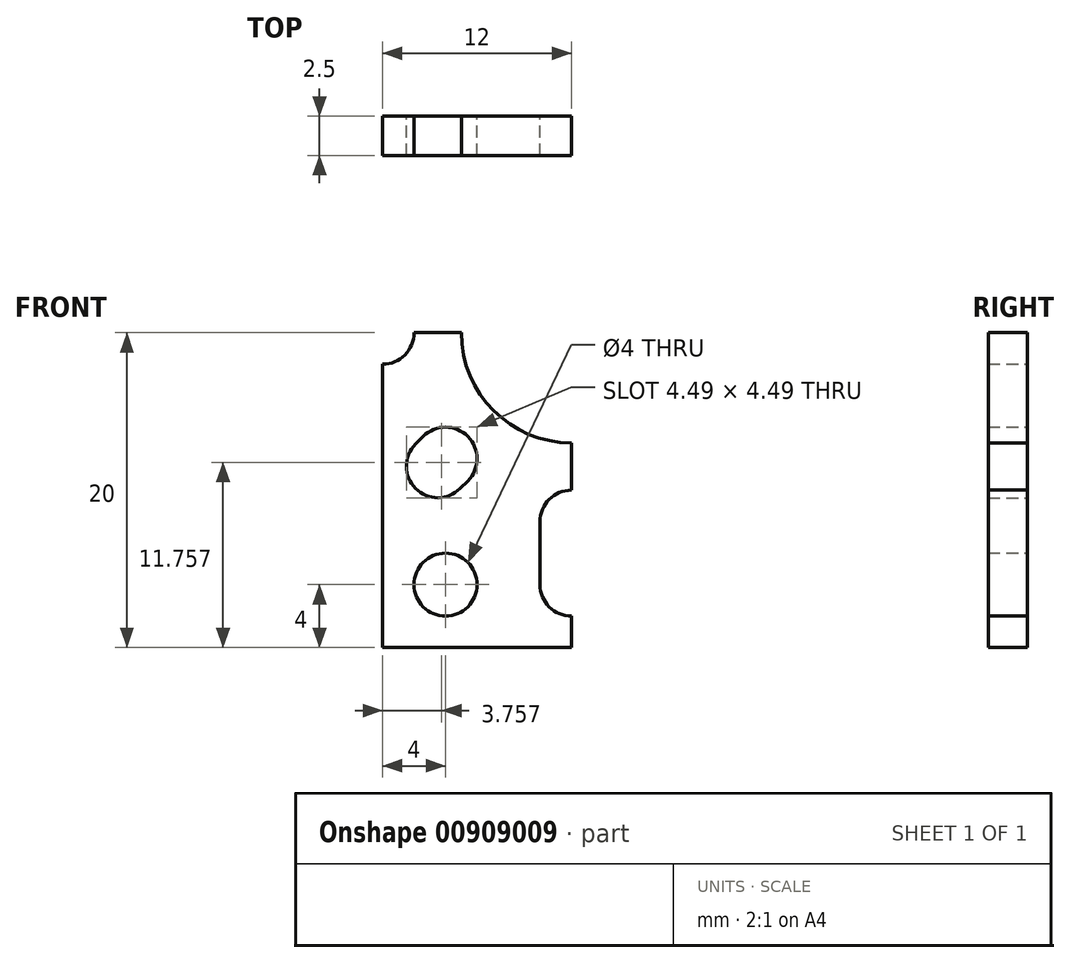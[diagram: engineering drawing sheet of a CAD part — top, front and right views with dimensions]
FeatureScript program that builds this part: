
annotation { "Feature Type Name" : "Feature", "Feature Type Description" : "" }
export const myFeature = defineFeature(function(context is Context, id is Id, definition is map)
    precondition{}
    {
        {
            var Q0;
            Q0=qCreatedBy(makeId("Front.planeOp"),FACE);
            var sketch = newSketch(context, id + "F0", { "sketchPlane" : qUnion([Q0])});
            skCircle(sketch, "E0", {"center": v(0, 0) * mm, "radius": 7 * mm});
            skArc(sketch, "E1", {"start": v(-2, 12) * mm, "mid": v(0, 10) * mm, "end": v(2, 12) * mm});
            skArc(sketch, "E2.1.0", {"start": v(-7.07, 9.9) * mm, "mid": v(-9.9, 9.9) * mm, "end": v(-9.9, 7.07) * mm});
            skArc(sketch, "E2.2.0", {"start": v(-12, -2) * mm, "mid": v(-10, 0) * mm, "end": v(-12, 2) * mm});
            skArc(sketch, "E2.4.0", {"start": v(2, -12) * mm, "mid": v(0, -10) * mm, "end": v(-2, -12) * mm});
            skArc(sketch, "E2.6.0", {"start": v(12, 2) * mm, "mid": v(10, 0) * mm, "end": v(12, -2) * mm});
            skArc(sketch, "E3", {"start": v(-9.41, 6.59) * mm, "mid": v(-6.59, 6.59) * mm, "end": v(-6.59, 9.41) * mm});
            skLineSegment(sketch, "E4", {"start": v(-9.9, 7.07) * mm, "end": v(-9.41, 6.59) * mm});
            skLineSegment(sketch, "E5", {"start": v(-7.07, 9.9) * mm, "end": v(-6.59, 9.41) * mm});
            skLineSegment(sketch, "E6.1.0", {"start": v(-7.07, -9.9) * mm, "end": v(-6.59, -9.41) * mm});
            skLineSegment(sketch, "E6.1.1", {"start": v(-9.9, -7.07) * mm, "end": v(-9.41, -6.59) * mm});
            skArc(sketch, "E6.1.2", {"start": v(-6.59, -9.41) * mm, "mid": v(-6.59, -6.59) * mm, "end": v(-9.41, -6.59) * mm});
            skArc(sketch, "E6.1.3", {"start": v(-9.9, -7.07) * mm, "mid": v(-9.9, -9.9) * mm, "end": v(-7.07, -9.9) * mm});
            skLineSegment(sketch, "E6.2.0", {"start": v(9.9, -7.07) * mm, "end": v(9.41, -6.59) * mm});
            skLineSegment(sketch, "E6.2.1", {"start": v(7.07, -9.9) * mm, "end": v(6.59, -9.41) * mm});
            skArc(sketch, "E6.2.2", {"start": v(9.41, -6.59) * mm, "mid": v(6.59, -6.59) * mm, "end": v(6.59, -9.41) * mm});
            skArc(sketch, "E6.2.3", {"start": v(7.07, -9.9) * mm, "mid": v(9.9, -9.9) * mm, "end": v(9.9, -7.07) * mm});
            skLineSegment(sketch, "E6.3.0", {"start": v(7.07, 9.9) * mm, "end": v(6.59, 9.41) * mm});
            skLineSegment(sketch, "E6.3.1", {"start": v(9.9, 7.07) * mm, "end": v(9.41, 6.59) * mm});
            skArc(sketch, "E6.3.2", {"start": v(6.59, 9.41) * mm, "mid": v(6.59, 6.59) * mm, "end": v(9.41, 6.59) * mm});
            skArc(sketch, "E6.3.3", {"start": v(9.9, 7.07) * mm, "mid": v(9.9, 9.9) * mm, "end": v(7.07, 9.9) * mm});
            skLineSegment(sketch, "E7.bottom", {"start": v(8, 16) * mm, "end": v(2, 16) * mm, "construction": true});
            skLineSegment(sketch, "E7.top", {"start": v(8, -16) * mm, "end": v(2, -16) * mm, "construction": true});
            skLineSegment(sketch, "E7.left", {"start": v(8, 16) * mm, "end": v(8, -16) * mm, "construction": true});
            skLineSegment(sketch, "E7.right", {"start": v(-8, 16) * mm, "end": v(-8, -16) * mm, "construction": true});
            skArc(sketch, "E8", {"start": v(2, 16) * mm, "mid": v(0, 18) * mm, "end": v(-2, 16) * mm});
            skArc(sketch, "E9", {"start": v(-2, -16) * mm, "mid": v(0, -18) * mm, "end": v(2, -16) * mm});
            skCircle(sketch, "E10", {"center": v(8, -16) * mm, "radius": 2 * mm});
            skCircle(sketch, "E11", {"center": v(-8, -16) * mm, "radius": 2 * mm});
            skCircle(sketch, "E12", {"center": v(-8, 16) * mm, "radius": 2 * mm});
            skCircle(sketch, "E13", {"center": v(8, 16) * mm, "radius": 2 * mm});
            skLineSegment(sketch, "E14.bottom", {"start": v(12, 20) * mm, "end": v(-12, 20) * mm});
            skLineSegment(sketch, "E14.top", {"start": v(12, -20) * mm, "end": v(-12, -20) * mm});
            skLineSegment(sketch, "E14.left", {"start": v(12, 20) * mm, "end": v(12, -20) * mm});
            skLineSegment(sketch, "E14.right", {"start": v(-12, 20) * mm, "end": v(-12, -20) * mm});
            skLineSegment(sketch, "E15.left", {"start": v(2, 12) * mm, "end": v(2, 16) * mm});
            skLineSegment(sketch, "E15.right", {"start": v(-2, 12) * mm, "end": v(-2, 16) * mm});
            skLineSegment(sketch, "E16.left", {"start": v(-2, -12) * mm, "end": v(-2, -16) * mm});
            skLineSegment(sketch, "E16.right", {"start": v(2, -12) * mm, "end": v(2, -16) * mm});
            skLineSegment(sketch, "E17.trimOffspring", {"start": v(-2, -16) * mm, "end": v(-8, -16) * mm, "construction": true});
            skLineSegment(sketch, "E18.trimOffspring", {"start": v(-2, 16) * mm, "end": v(-8, 16) * mm, "construction": true});
            skSolve(sketch);
        }
        {
            var Q0;
            Q0=makeQuery(id+"F0.imprint","IMPRINT",FACE,{"disambiguationData":[TD([[makeQuery(id+"F0.imprint","IMPRINT",EDGE,{"derivedFrom":sQuery(id+"F0.wireOp",EDGE,"E0")}),-1.0]])]});
            extrude(context, id + "F1", {"entities" : qUnion([Q0]), "depth" : 2.5 * mm, "offsetDistance" : 25 * mm});
        }
        {
            var Q0;
            Q0=makeQuery(id+"F1.opExtrude","CAP_FACE",FACE,{"disambiguationData":[OSD([sQuery(id+"F0.wireOp",EDGE,"E0"),sQuery(id+"F0.wireOp",EDGE,"E1"),sQuery(id+"F0.wireOp",EDGE,"E2.1.0"),sQuery(id+"F0.wireOp",EDGE,"E2.2.0"),sQuery(id+"F0.wireOp",EDGE,"E2.4.0"),sQuery(id+"F0.wireOp",EDGE,"E2.6.0"),sQuery(id+"F0.wireOp",EDGE,"E3"),sQuery(id+"F0.wireOp",EDGE,"E4"),sQuery(id+"F0.wireOp",EDGE,"E5"),sQuery(id+"F0.wireOp",EDGE,"E6.1.0"),sQuery(id+"F0.wireOp",EDGE,"E6.1.1"),sQuery(id+"F0.wireOp",EDGE,"E6.1.2"),sQuery(id+"F0.wireOp",EDGE,"E6.1.3"),sQuery(id+"F0.wireOp",EDGE,"E6.2.0"),sQuery(id+"F0.wireOp",EDGE,"E6.2.1"),sQuery(id+"F0.wireOp",EDGE,"E6.2.2"),sQuery(id+"F0.wireOp",EDGE,"E6.2.3"),sQuery(id+"F0.wireOp",EDGE,"E6.3.0"),sQuery(id+"F0.wireOp",EDGE,"E6.3.1"),sQuery(id+"F0.wireOp",EDGE,"E6.3.2"),sQuery(id+"F0.wireOp",EDGE,"E6.3.3"),sQuery(id+"F0.wireOp",EDGE,"E8"),sQuery(id+"F0.wireOp",EDGE,"E9"),sQuery(id+"F0.wireOp",EDGE,"E10"),sQuery(id+"F0.wireOp",EDGE,"E11"),sQuery(id+"F0.wireOp",EDGE,"E12"),sQuery(id+"F0.wireOp",EDGE,"E13"),sQuery(id+"F0.wireOp",EDGE,"E14.bottom"),sQuery(id+"F0.wireOp",EDGE,"E14.top"),sQuery(id+"F0.wireOp",EDGE,"E14.left"),sQuery(id+"F0.wireOp",EDGE,"E14.right"),sQuery(id+"F0.wireOp",EDGE,"E15.left"),sQuery(id+"F0.wireOp",EDGE,"E15.right"),sQuery(id+"F0.wireOp",EDGE,"E16.left"),sQuery(id+"F0.wireOp",EDGE,"E16.right")])],"isStart":false});
            var sketch = newSketch(context, id + "F2", { "sketchPlane" : qUnion([Q0])});
            skLineSegment(sketch, "E19.bottom", {"start": v(0, 0) * mm, "end": v(-15.09, 0) * mm});
            skLineSegment(sketch, "E19.top", {"start": v(0, -23.57) * mm, "end": v(-15.09, -23.57) * mm});
            skLineSegment(sketch, "E19.left", {"start": v(0, 0) * mm, "end": v(0, -23.57) * mm});
            skLineSegment(sketch, "E19.right", {"start": v(-15.09, 0) * mm, "end": v(-15.09, -23.57) * mm});
            skSolve(sketch);
        }
        {
            var Q0;
            Q0 = qSketchRegion(id + "F2", true);
            extrude(context, id + "F3", {"entities" : qUnion([Q0]), "operationType" : NewBodyOperationType.INTERSECT, "oppositeDirection" : true, "depth" : 25 * mm, "offsetDistance" : 25 * mm});
        }
    });
